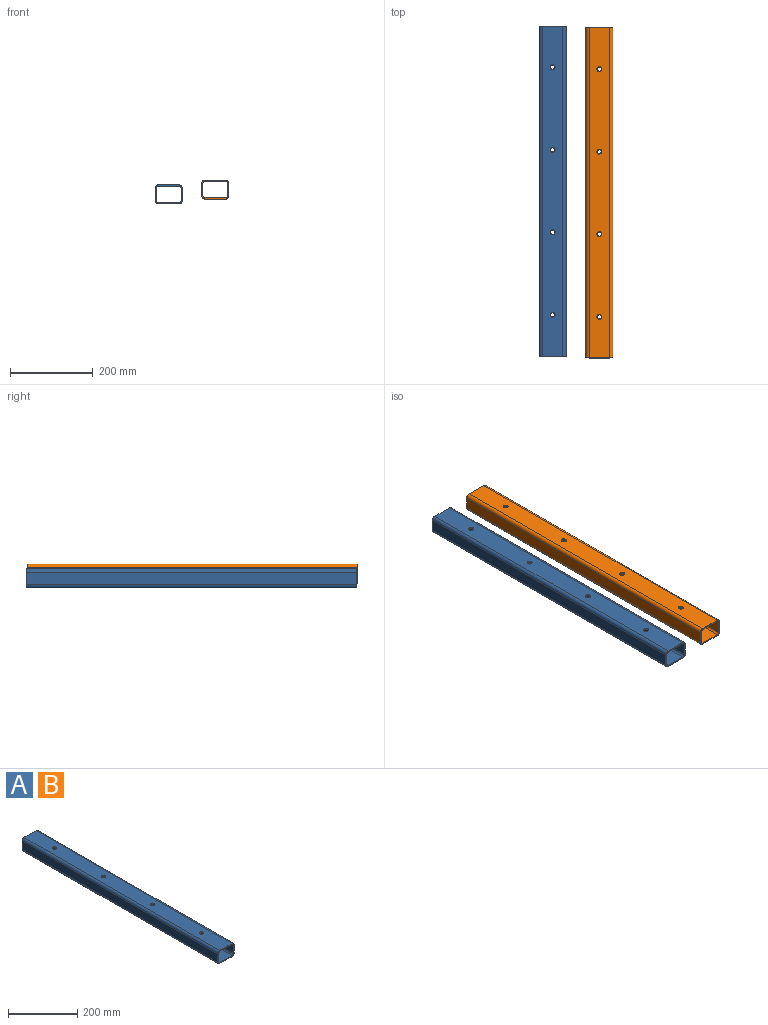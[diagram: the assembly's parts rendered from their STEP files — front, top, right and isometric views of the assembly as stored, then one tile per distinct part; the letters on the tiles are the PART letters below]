
ASSEMBLY  parts=2 mates=1
PART A: 26 faces, bbox 66x800x46 mm
  f0: plane 66x46mm, normal (0,-1,0), area 602.5mm2, adj f2,f3,f4,f5,f6,f7,f8,f9
  f1: plane 66x46mm, normal (0,1,0), area 602.5mm2, adj f2,f3,f4,f5,f6,f7,f8,f9
  f2: plane 800x50mm, normal (0,0,1), area 39547.6mm2, adj f0,f1,f6,f9,f18,f19,f20,f21
  f3: plane 800x30mm, normal (-1,0,0), area 24000mm2, adj f0,f1,f6,f7
  f4: plane 800x50mm, normal (0,0,-1), area 39685.8mm2, adj f0,f1,f7,f8,f22,f23,f24,f25
  f5: plane 800x30mm, normal (1,0,0), area 24000mm2, adj f0,f1,f8,f9
  f6: cylinder r=8mm len=800mm, axis (0,-1,0), area 10053.1mm2, adj f0,f1,f2,f3
  f7: cylinder r=8mm len=800mm, axis (0,1,0), area 10053.1mm2, adj f0,f1,f3,f4
  f8: cylinder r=8mm len=800mm, axis (0,-1,0), area 10053.1mm2, adj f0,f1,f4,f5
  f9: cylinder r=8mm len=800mm, axis (0,1,0), area 10053.1mm2, adj f0,f1,f2,f5
  f10: plane 800x50mm, normal (0,0,-1), area 39547.6mm2, adj f0,f1,f14,f17,f18,f19,f20,f21
  f11: plane 800x30mm, normal (1,0,0), area 24000mm2, adj f0,f1,f14,f15
  f12: plane 800x50mm, normal (0,0,1), area 39685.8mm2, adj f0,f1,f15,f16,f22,f23,f24,f25
  f13: plane 800x30mm, normal (-1,0,0), area 24000mm2, adj f0,f1,f16,f17
  f14: cylinder r=5mm len=800mm, axis (0,-1,0), area 6283.2mm2, adj f0,f1,f10,f11
  f15: cylinder r=5mm len=800mm, axis (0,1,0), area 6283.2mm2, adj f0,f1,f11,f12
  f16: cylinder r=5mm len=800mm, axis (0,-1,0), area 6283.2mm2, adj f0,f1,f12,f13
  f17: cylinder r=5mm len=800mm, axis (0,1,0), area 6283.2mm2, adj f0,f1,f10,f13
  f18: cylinder r=6mm len=12mm, axis (0,0,1), area 113.1mm2, adj f2,f10
  f19: cylinder r=6mm len=12mm, axis (0,0,1), area 113.1mm2, adj f2,f10
  f20: cylinder r=6mm len=12mm, axis (0,0,1), area 113.1mm2, adj f2,f10
  f21: cylinder r=6mm len=12mm, axis (0,0,1), area 113.1mm2, adj f2,f10
  f22: cylinder r=5mm len=10mm, axis (0,0,-1), area 94.2mm2, adj f4,f12
  f23: cylinder r=5mm len=10mm, axis (0,0,-1), area 94.2mm2, adj f4,f12
  f24: cylinder r=5mm len=10mm, axis (0,0,-1), area 94.2mm2, adj f4,f12
  f25: cylinder r=5mm len=10mm, axis (0,0,-1), area 94.2mm2, adj f4,f12
PART B: same geometry as A
PLACE A t=(-276.23,229.5,-161.44)mm
PLACE B t=(-163,224.99,-149.5)mm
MATE parallel A.f5 <-> B.f3  axis (1,0,0) through (-243.23,-170.5,-161.44)mm
